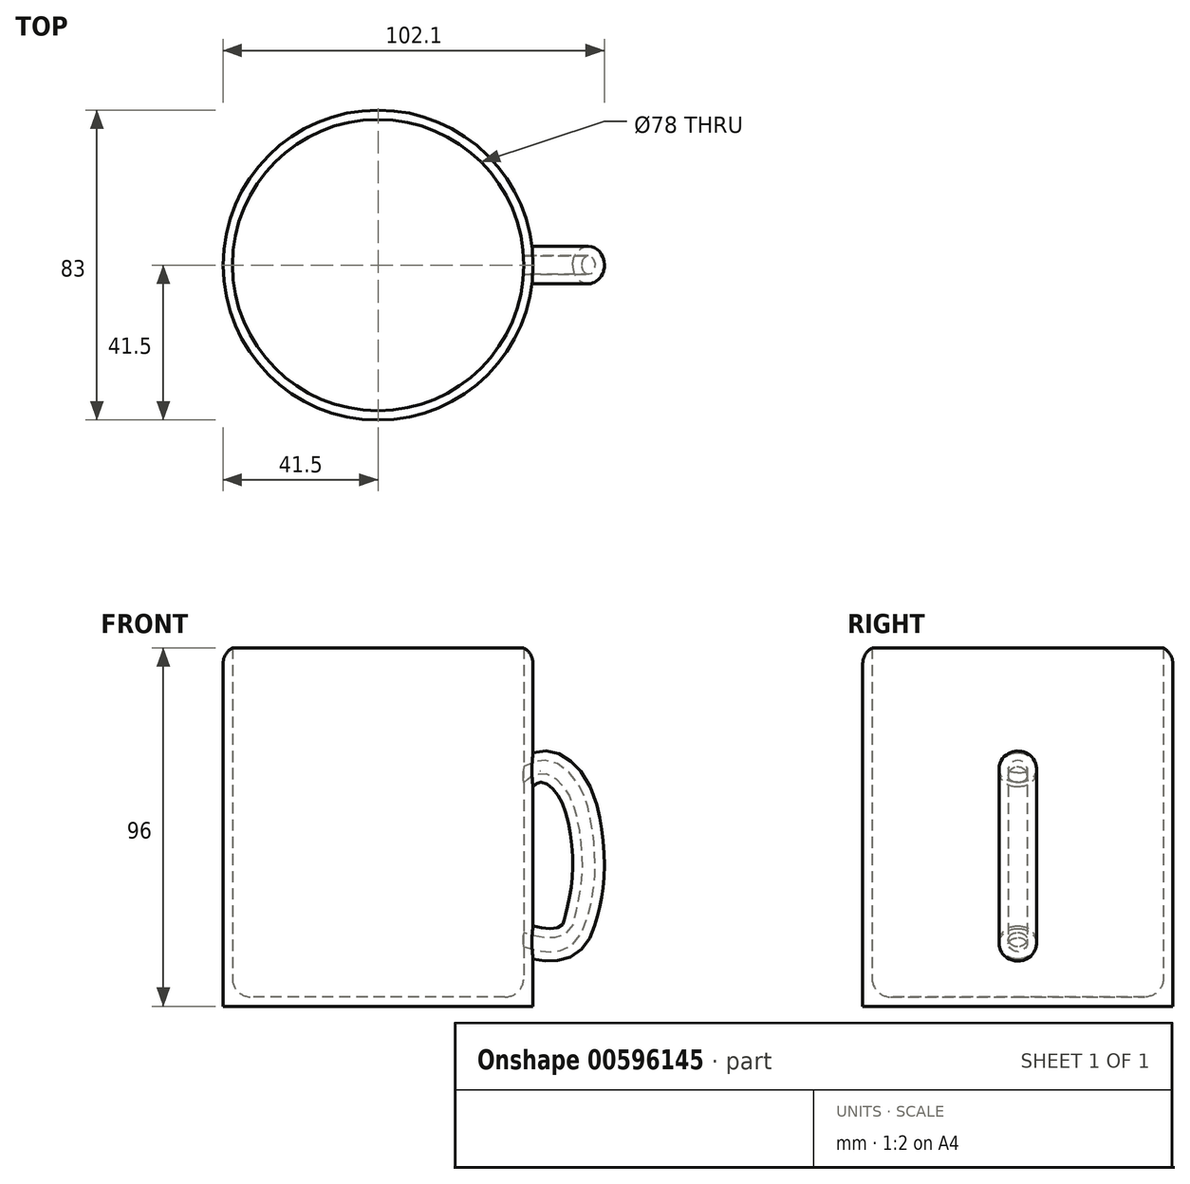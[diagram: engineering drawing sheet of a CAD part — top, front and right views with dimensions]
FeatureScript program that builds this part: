
annotation { "Feature Type Name" : "Feature", "Feature Type Description" : "" }
export const myFeature = defineFeature(function(context is Context, id is Id, definition is map)
    precondition{}
    {
        {
            var Q0;
            Q0=qCreatedBy(makeId("Top.planeOp"),FACE);
            var sketch = newSketch(context, id + "F0", { "sketchPlane" : qUnion([Q0])});
            skCircle(sketch, "E0", {"center": v(0, 0) * mm, "radius": 41.5 * mm});
            skSolve(sketch);
        }
        {
            var Q0;
            Q0 = qSketchRegion(id + "F0", true);
            extrude(context, id + "F1", {"entities" : qUnion([Q0]), "depth" : 96 * mm, "offsetDistance" : 25 * mm});
        }
        {
            var Q0;
            Q0=qCreatedBy(makeId("Front.planeOp"),FACE);
            var sketch = newSketch(context, id + "F2", { "sketchPlane" : qUnion([Q0])});
            skFitSpline(sketch, "E1", {"points": [v(36.5, 58.04) * mm, v(39.84, 60.97) * mm, v(45.07, 62.43) * mm, v(50.72, 58.04) * mm, v(54.07, 48.84) * mm, v(55.11, 36.5) * mm, v(53.65, 26.25) * mm, v(50.1, 19.14) * mm, v(43.2, 18.1) * mm, v(35.24, 20.6) * mm], "startDerivative": vector(36.1, 36.87) * mm, "endDerivative": vector(-68.56, 27.31) * mm});
            skSolve(sketch);
        }
        {
            var Q0;
            Q0=qCreatedBy(makeId("Right.planeOp"),FACE);
            cPlane(context, id + "F3", {"entities" : qUnion([Q0]), "cplaneType" : CPlaneType.OFFSET, "offset" : 40 * mm, "width" : 150 * mm, "height" : 150 * mm});
        }
        {
            var Q0;
            Q0=qCreatedBy(id+"F3.planeOp",FACE);
            var sketch = newSketch(context, id + "F4", { "sketchPlane" : qUnion([Q0])});
            skCircle(sketch, "E2", {"center": v(0, 62.43) * mm, "radius": 5 * mm});
            skSolve(sketch);
        }
        {
            var Q0;
            Q0 = qSketchRegion(id + "F4", true);
            var Q1;
            Q1 = qConstructionFilter(qBodyType(qCreatedBy(id + "F2" ,EDGE), BodyType.WIRE), ConstructionObject.NO);
            sweep(context, id + "F5", {"operationType" : NewBodyOperationType.ADD, "profiles" : qUnion([Q0]), "path" : qUnion([Q1])});
        }
        {
            var Q0;
            Q0=makeQuery(id+"F1.opExtrude","CAP_FACE",FACE,{"disambiguationData":[OSD([sQuery(id+"F0.wireOp",EDGE,"E0")])],"isStart":false});
            shell(context, id + "F6", {"entities" : qUnion([Q0]), "thickness" : 2.5 * mm});
        }
        {
            var Q0;
            Q0=makeQuery(id+"F1.opExtrude","CAP_EDGE",EDGE,{"disambiguationData":[OSD([sQuery(id+"F0.wireOp",EDGE,"E0")])],"isStart":false});
            fillet(context, id + "F7", {"entities" : qUnion([Q0]), "radius" : 5 * mm, "tangentPropagation" : true, "allowEdgeOverflow" : false});
        }
        {
            var Q0;
            {var subQ0=sQuery(id+"F0.wireOp",EDGE,"E0");Q0=makeQuery(id+"F6.opShell","OFFSET_EDGE",EDGE,{"disambiguationData":[OSD([subQ0]),TDD([makeQuery(id+"F1.opExtrude","CAP_EDGE",EDGE,{"disambiguationData":[OSD([subQ0])],"isStart":true})])]});}
            fillet(context, id + "F8", {"entities" : qUnion([Q0]), "radius" : 5 * mm, "tangentPropagation" : true, "allowEdgeOverflow" : false});
        }
    });
